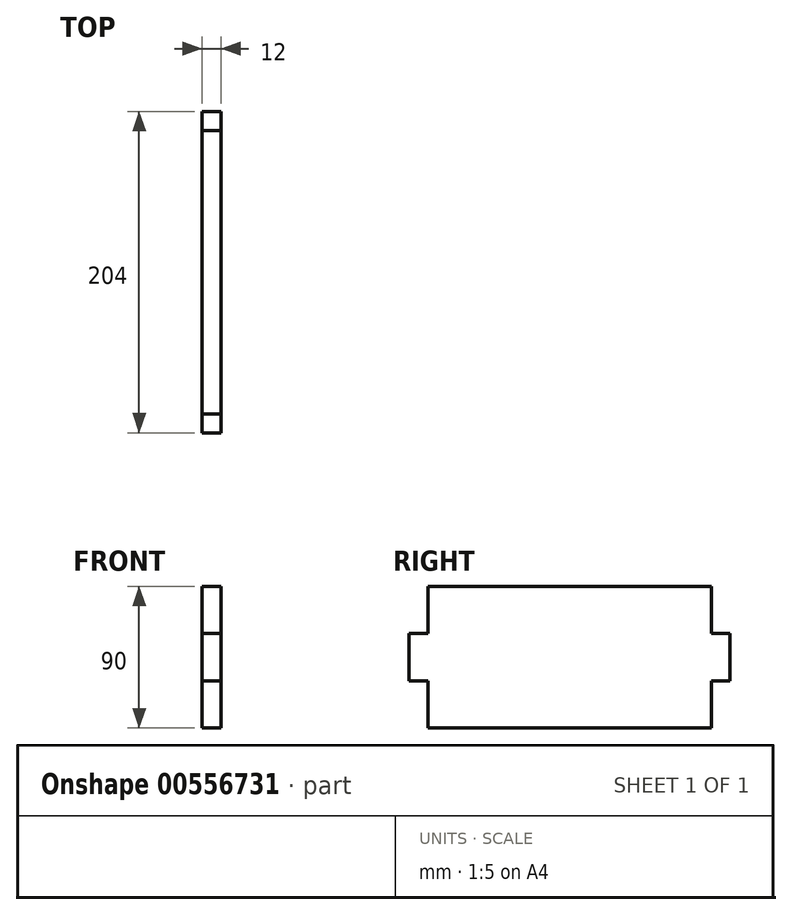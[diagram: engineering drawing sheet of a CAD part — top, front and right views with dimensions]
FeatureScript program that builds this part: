
annotation { "Feature Type Name" : "Feature", "Feature Type Description" : "" }
export const myFeature = defineFeature(function(context is Context, id is Id, definition is map)
    precondition{}
    {
        {
            var Q0;
            Q0=qCreatedBy(makeId("Right.planeOp"),FACE);
            var sketch = newSketch(context, id + "F0", { "sketchPlane" : qUnion([Q0])});
            skLineSegment(sketch, "E0", {"start": v(0, 0) * mm, "end": v(0, 30) * mm});
            skLineSegment(sketch, "E1", {"start": v(-12, 30) * mm, "end": v(0, 30) * mm});
            skLineSegment(sketch, "E2", {"start": v(-12, 30) * mm, "end": v(-12, 60) * mm});
            skLineSegment(sketch, "E3", {"start": v(0, 60) * mm, "end": v(-12, 60) * mm});
            skLineSegment(sketch, "E4", {"start": v(0, 60) * mm, "end": v(0, 90) * mm});
            skLineSegment(sketch, "E5", {"start": v(0, 90) * mm, "end": v(0, 0) * mm});
            skLineSegment(sketch, "E6", {"start": v(90, 0) * mm, "end": v(0, 0) * mm});
            skLineSegment(sketch, "E7", {"start": v(0, 90) * mm, "end": v(90, 90) * mm});
            skLineSegment(sketch, "E8", {"start": v(90, 90) * mm, "end": v(90, 0) * mm, "construction": true});
            skLineSegment(sketch, "E9.MirrorCS", {"start": v(180, 60) * mm, "end": v(180, 90) * mm});
            skLineSegment(sketch, "E10.MirrorCS", {"start": v(180, 0) * mm, "end": v(180, 30) * mm});
            skLineSegment(sketch, "E11.MirrorCS", {"start": v(192, 30) * mm, "end": v(180, 30) * mm});
            skLineSegment(sketch, "E12.MirrorCS", {"start": v(192, 30) * mm, "end": v(192, 60) * mm});
            skLineSegment(sketch, "E13.MirrorCS", {"start": v(180, 60) * mm, "end": v(192, 60) * mm});
            skLineSegment(sketch, "E14.MirrorCS", {"start": v(90, 0) * mm, "end": v(180, 0) * mm});
            skLineSegment(sketch, "E15.MirrorCS", {"start": v(180, 90) * mm, "end": v(180, 0) * mm});
            skLineSegment(sketch, "E16.MirrorCS", {"start": v(180, 90) * mm, "end": v(90, 90) * mm});
            skSolve(sketch);
        }
        {
            var Q0;
            {var subQ4=sQuery(id+"F0.wireOp",EDGE,"E7");Q0=makeQuery(id+"F0.imprint","IMPRINT",FACE,{"disambiguationData":[TD([[makeQuery(id+"F0.imprint","IMPRINT",EDGE,{"derivedFrom":subQ4}),-1.0]])]});}
            var Q1;
            {var subQ0=sQuery(id+"F0.wireOp",EDGE,"E1");Q1=makeQuery(id+"F0.imprint","IMPRINT",FACE,{"disambiguationData":[TD([[makeQuery(id+"F0.imprint","IMPRINT",EDGE,{"derivedFrom":subQ0}),1.0]])]});}
            var Q2;
            {var subQ0=sQuery(id+"F0.wireOp",EDGE,"E11.MirrorCS");Q2=makeQuery(id+"F0.imprint","IMPRINT",FACE,{"disambiguationData":[TD([[makeQuery(id+"F0.imprint","IMPRINT",EDGE,{"derivedFrom":subQ0}),-1.0]])]});}
            extrude(context, id + "F1", {"entities" : qUnion([Q0, Q1, Q2]), "endBound" : BoundingType.SYMMETRIC, "depth" : 12 * mm, "offsetDistance" : 25 * mm});
        }
        {
            var Q0;
            Q0 = qSketchRegion(id + "F0", true);
            extrude(context, id + "F2", {"entities" : qUnion([Q0]), "operationType" : NewBodyOperationType.ADD, "endBound" : BoundingType.SYMMETRIC, "depth" : 12 * mm, "offsetDistance" : 25 * mm});
        }
    });
